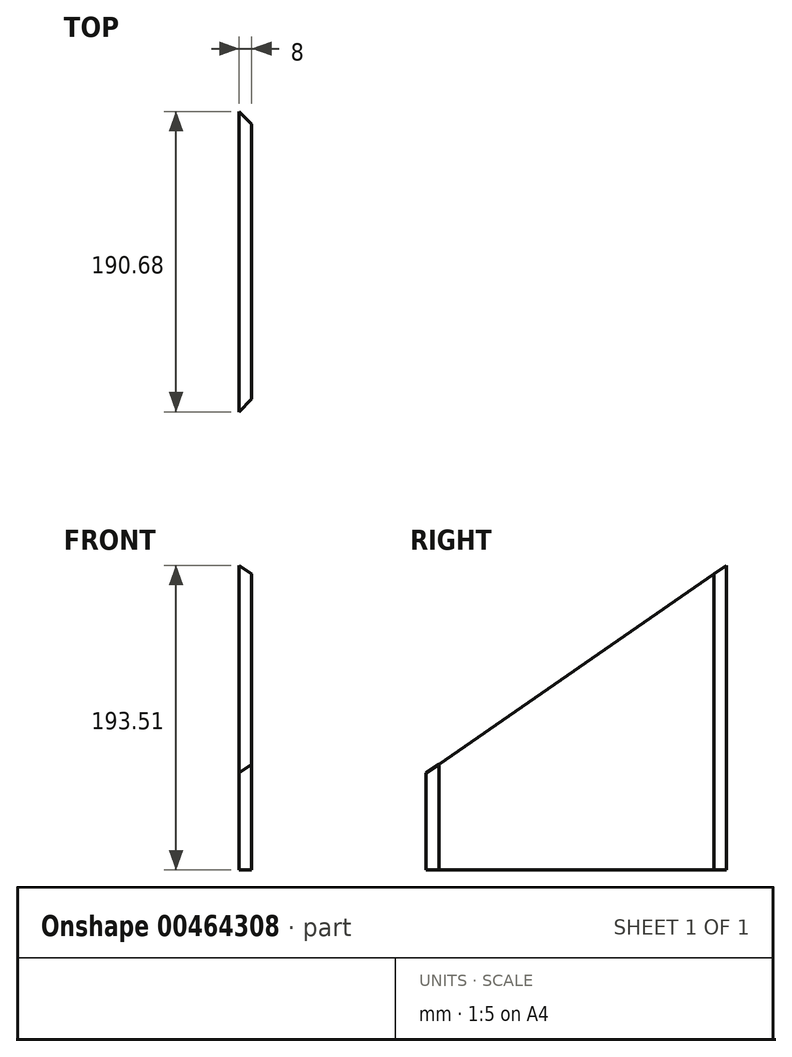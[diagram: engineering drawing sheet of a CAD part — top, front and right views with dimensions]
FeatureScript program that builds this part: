
annotation { "Feature Type Name" : "Feature", "Feature Type Description" : "" }
export const myFeature = defineFeature(function(context is Context, id is Id, definition is map)
    precondition{}
    {
        {
            var Q0;
            Q0=qCreatedBy(makeId("Right.planeOp"),FACE);
            var sketch = newSketch(context, id + "F0", { "sketchPlane" : qUnion([Q0])});
            skLineSegment(sketch, "E0.top", {"start": v(-99.98, -89.5) * mm, "end": v(95.02, -89.5) * mm});
            skPoint(sketch, "E0.middle", {"position": v(0, 0) * mm});
            skLineSegment(sketch, "E1", {"start": v(-99.98, -89.5) * mm, "end": v(-99.98, -29.5) * mm});
            skLineSegment(sketch, "E2", {"start": v(95.02, -89.5) * mm, "end": v(95.02, 105.5) * mm});
            skLineSegment(sketch, "E3", {"start": v(95.02, 105.5) * mm, "end": v(-99.98, -29.5) * mm});
            skSolve(sketch);
        }
        {
            var Q0;
            Q0=qSketchRegion(id+"F0",true);
            extrude(context, id + "F1", {"entities" : qUnion([Q0]), "endBound" : BoundingType.SYMMETRIC, "depth" : 8 * mm});
        }
        {
            var Q0;
            Q0=makeQuery(id+"F1.opExtrude","CAP_EDGE",EDGE,{"disambiguationData":[OSD([sQuery(id+"F0.wireOp",EDGE,"E1")])],"isStart":false});
            chamfer(context, id + "F2", {"entities" : qUnion([Q0]), "width" : 10.16 * mm, "tangentPropagation" : true});
        }
        {
            var Q0;
            Q0=makeQuery(id+"F1.opExtrude","CAP_EDGE",EDGE,{"disambiguationData":[OSD([sQuery(id+"F0.wireOp",EDGE,"E2")])],"isStart":false});
            chamfer(context, id + "F3", {"entities" : qUnion([Q0]), "width" : 10.16 * mm, "tangentPropagation" : true});
        }
    });
